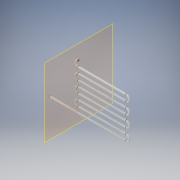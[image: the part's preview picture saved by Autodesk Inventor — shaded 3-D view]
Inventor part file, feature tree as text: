
AUTODESK INVENTOR PART (.ipt)
format: ipt  version: 2019.4 (Build 234330000, 330)  size: 230,912 bytes
history: native  units: mm
features: sketch x4, other x3, sweep x1, pattern_linear x1, extrude x1
ambient origin geometry x8: Origin, YZ Plane, XZ Plane, XY Plane, X Axis, Y Axis, Z Axis, Center Point
bodies: Body1 (feature_tree)
feature tree (10):
  other  "Sólido1"
  sketch  "Esboço3"  dims[d21=50.0mm d23=50.0mm]
  other  "Plano de trabalho3"
  sweep  "Varredura1"
  pattern_linear  "Padrão retangular1"  Count1=5  [1 undecoded]
  sketch  "Esboço 3D1"  dims[d18=1000.0mm d19=1000.0mm d20=50.0mm]
  extrude  "Extrusão1"  Depth=50.0mm
  sketch  "Esboço5"  dims[d24=80.0mm]
  sketch  "Esboço6"  dims[d25=80.0mm d26=40.0mm d28=200.0mm d29=10.0mm d31=10.0mm d33=80.0mm d36=19.05mm d37=6.0mm d38=0.0mm d39=0.0mm d40=40.0mm d42=200.0mm d43=500.0mm d44=0.0mm]
  other  "Contorno projetado1"
note: 1 required parameter value undecoded (feature->parameter linkage not recoverable at this tier; creation-order binding heuristic only, values carry confidence <= 0.55)
